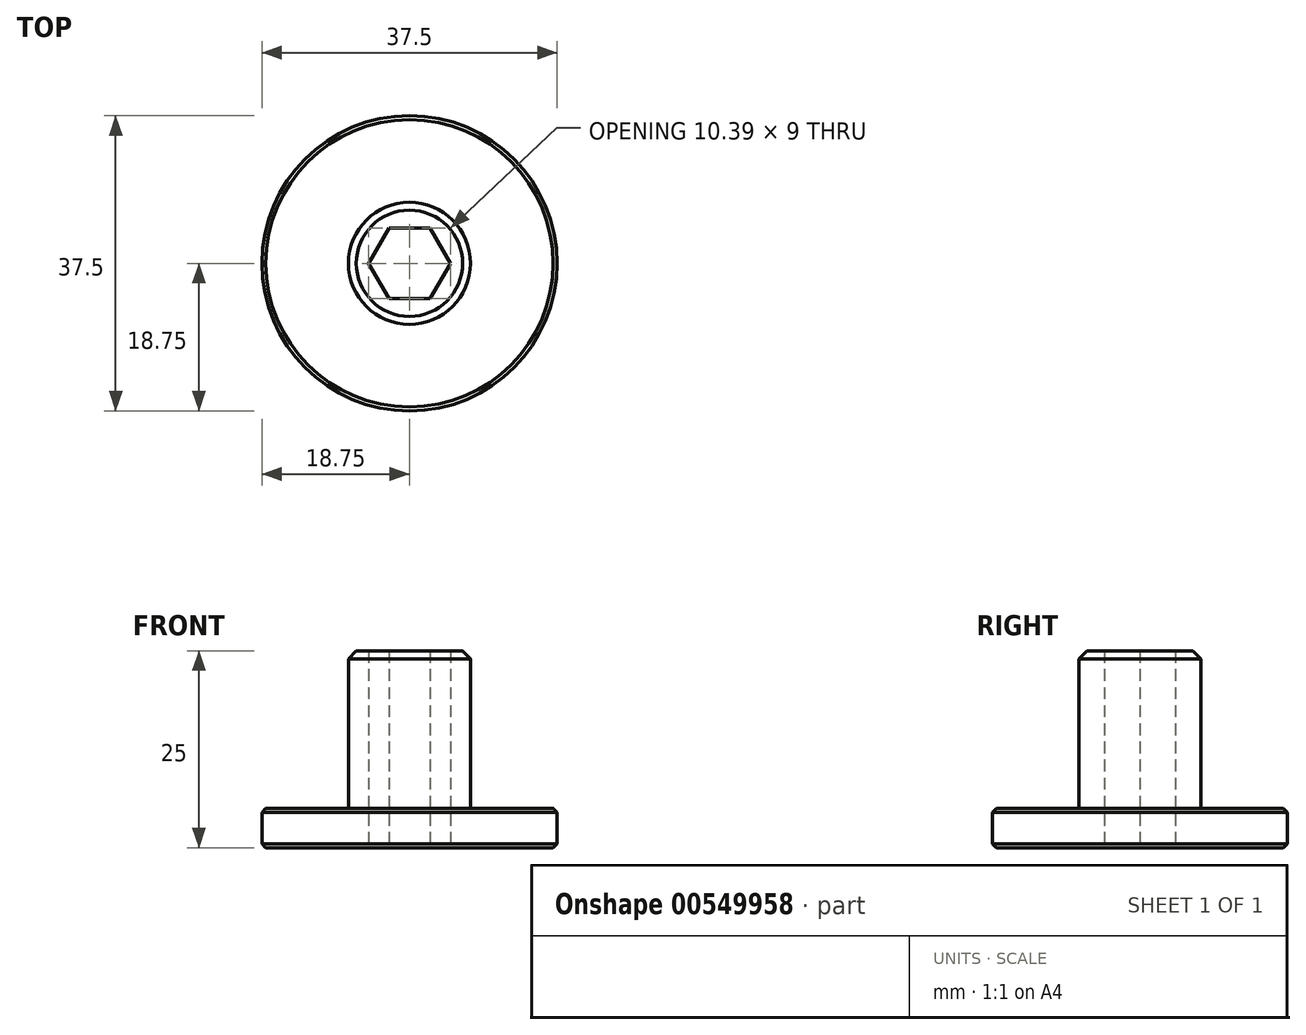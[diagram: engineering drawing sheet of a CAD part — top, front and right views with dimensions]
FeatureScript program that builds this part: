
annotation { "Feature Type Name" : "Feature", "Feature Type Description" : "" }
export const myFeature = defineFeature(function(context is Context, id is Id, definition is map)
    precondition{}
    {
        {
            var Q0;
            Q0=qCreatedBy(makeId("Top.planeOp"),FACE);
            var sketch = newSketch(context, id + "F0", { "sketchPlane" : qUnion([Q0])});
            skCircle(sketch, "E0.cCircle", {"center": v(0, 0) * mm, "radius": 4.5 * mm, "construction": true});
            skLineSegment(sketch, "E0.0", {"start": v(5.2, 0) * mm, "end": v(2.6, -4.5) * mm});
            skLineSegment(sketch, "E0.1", {"start": v(2.6, -4.5) * mm, "end": v(-2.6, -4.5) * mm});
            skLineSegment(sketch, "E0.2", {"start": v(-2.6, -4.5) * mm, "end": v(-5.2, 0) * mm});
            skLineSegment(sketch, "E0.3", {"start": v(-5.2, 0) * mm, "end": v(-2.6, 4.5) * mm});
            skLineSegment(sketch, "E0.4", {"start": v(-2.6, 4.5) * mm, "end": v(2.6, 4.5) * mm});
            skLineSegment(sketch, "E0.5", {"start": v(2.6, 4.5) * mm, "end": v(5.2, 0) * mm});
            skPoint(sketch, "E0.0.midPoint", {"position": v(3.9, -2.25) * mm});
            skCircle(sketch, "E1", {"center": v(0, 0) * mm, "radius": 18.75 * mm});
            skSolve(sketch);
        }
        {
            var Q0;
            Q0 = qSketchRegion(id + "F0", true);
            extrude(context, id + "F1", {"entities" : qUnion([Q0]), "depth" : 5 * mm, "offsetDistance" : 25 * mm});
        }
        {
            var Q0;
            Q0=makeQuery(id+"F1.opExtrude","CAP_FACE",FACE,{"disambiguationData":[OSD([sQuery(id+"F0.wireOp",EDGE,"E0.0"),sQuery(id+"F0.wireOp",EDGE,"E0.1"),sQuery(id+"F0.wireOp",EDGE,"E0.2"),sQuery(id+"F0.wireOp",EDGE,"E0.3"),sQuery(id+"F0.wireOp",EDGE,"E0.4"),sQuery(id+"F0.wireOp",EDGE,"E0.5"),sQuery(id+"F0.wireOp",EDGE,"E1")])],"isStart":false});
            var sketch = newSketch(context, id + "F2", { "sketchPlane" : qUnion([Q0])});
            skCircle(sketch, "E2", {"center": v(0, 0) * mm, "radius": 7.75 * mm});
            skSolve(sketch);
        }
        {
            var Q0;
            Q0=makeQuery(id+"F2.imprint","IMPRINT",FACE,{"disambiguationData":[TD([[makeQuery(id+"F2.imprint","IMPRINT",EDGE,{"derivedFrom":sQuery(id+"F2.wireOp",EDGE,"E2")}),1.0]])]});
            extrude(context, id + "F3", {"entities" : qUnion([Q0]), "operationType" : NewBodyOperationType.ADD, "depth" : 20 * mm, "offsetDistance" : 25 * mm});
        }
        {
            var Q0;
            Q0=makeQuery(id+"F1.opExtrude","CAP_EDGE",EDGE,{"disambiguationData":[OSD([sQuery(id+"F0.wireOp",EDGE,"E1")])],"isStart":true});
            var Q1;
            Q1=makeQuery(id+"F1.opExtrude","CAP_EDGE",EDGE,{"disambiguationData":[OSD([sQuery(id+"F0.wireOp",EDGE,"E1")])],"isStart":false});
            chamfer(context, id + "F4", {"entities" : qUnion([Q0, Q1]), "width" : 0.5 * mm, "tangentPropagation" : true});
        }
        {
            var Q0;
            Q0=makeQuery(id+"F3.opExtrude","CAP_EDGE",EDGE,{"disambiguationData":[OSD([sQuery(id+"F2.wireOp",EDGE,"E2")])],"isStart":false});
            chamfer(context, id + "F5", {"entities" : qUnion([Q0]), "width" : 1 * mm, "tangentPropagation" : true});
        }
    });
